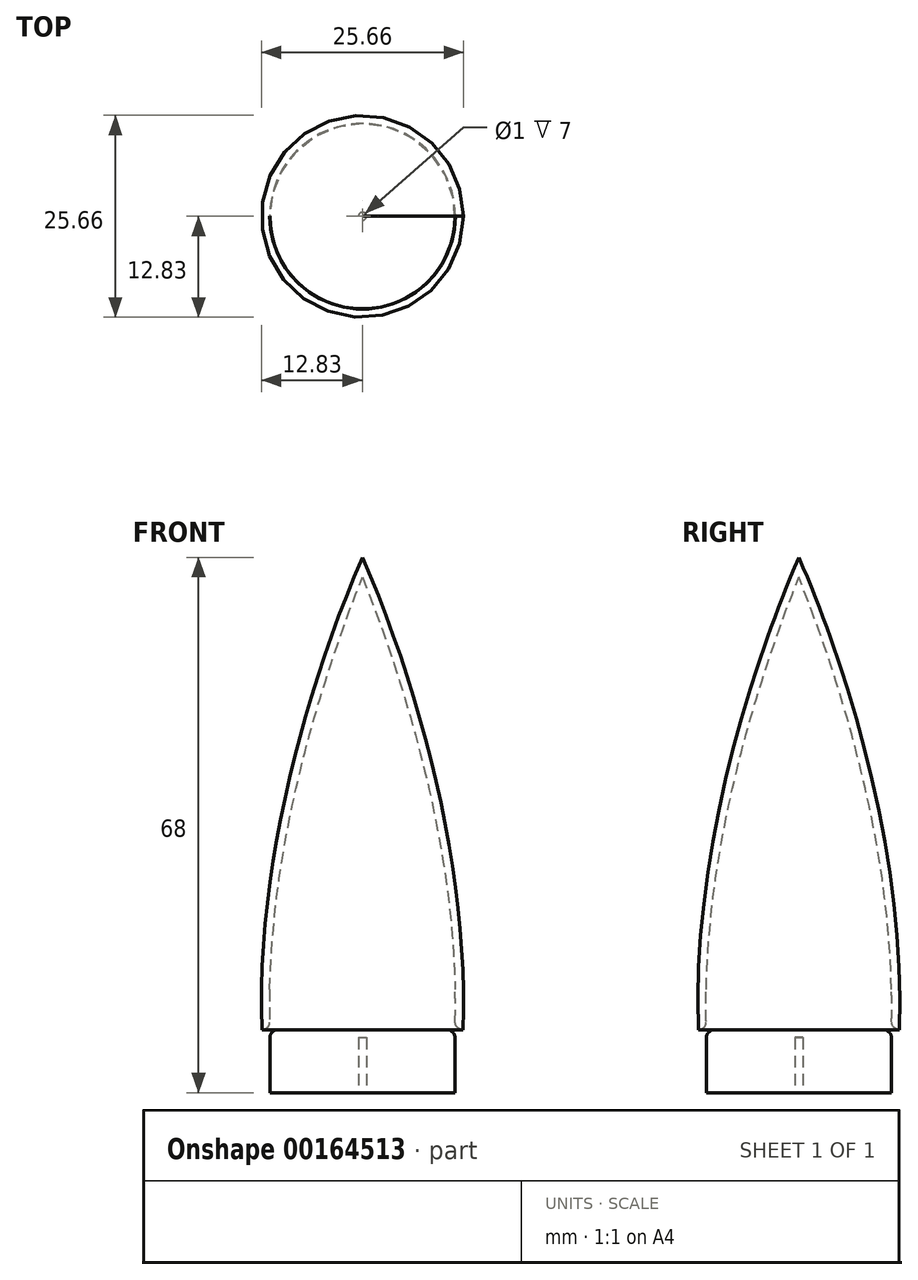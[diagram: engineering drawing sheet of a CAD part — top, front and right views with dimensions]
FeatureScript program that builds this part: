
annotation { "Feature Type Name" : "Feature", "Feature Type Description" : "" }
export const myFeature = defineFeature(function(context is Context, id is Id, definition is map)
    precondition{}
    {
        {
            var Q0;
            Q0=qCreatedBy(makeId("Front.planeOp"),FACE);
            var sketch = newSketch(context, id + "F0", { "sketchPlane" : qUnion([Q0])});
            skPoint(sketch, "E0.0", {"position": v(0, 0) * mm});
            skPoint(sketch, "E1.endSnap0", {"position": v(0, 8) * mm});
            skFitSpline(sketch, "E2", {"points": [v(0, 68) * mm, v(12.75, 8) * mm], "startDerivative": vector(23.82, -54.9) * mm, "endDerivative": vector(-2.44, -56.68) * mm});
            skLineSegment(sketch, "E3", {"start": v(6.61, 8) * mm, "end": v(12.75, 8) * mm});
            skLineSegment(sketch, "E4", {"start": v(0, 8) * mm, "end": v(6.77, 8) * mm});
            skLineSegment(sketch, "E5", {"start": v(11.75, 8) * mm, "end": v(11.75, 0) * mm});
            skLineSegment(sketch, "E6", {"start": v(11.75, 0) * mm, "end": v(0.5, 0) * mm});
            skLineSegment(sketch, "E7", {"start": v(0, 8) * mm, "end": v(0, 7) * mm});
            skLineSegment(sketch, "E8", {"start": v(0, 65.49) * mm, "end": v(0, 68) * mm});
            skFitSpline(sketch, "E9", {"points": [v(0, 65.49) * mm, v(11.75, 8) * mm], "startDerivative": vector(21.48, -54.4) * mm, "endDerivative": vector(-1.7, -57.32) * mm});
            skArc(sketch, "E10.filletArc", {"start": v(6.77, 8) * mm, "mid": v(10.34, 9.5) * mm, "end": v(11.77, 13.1) * mm});
            skLineSegment(sketch, "E11", {"start": v(0, 8) * mm, "end": v(0, 65.49) * mm, "construction": true});
            skLineSegment(sketch, "E12", {"start": v(0, 7) * mm, "end": v(0.5, 7) * mm});
            skLineSegment(sketch, "E13", {"start": v(0.5, 7) * mm, "end": v(0.5, 0) * mm});
            skSolve(sketch);
        }
        {
            var Q0;
            {var subQ1=sQuery(id+"F0.wireOp",EDGE,"E2");Q0=makeQuery(id+"F0.imprint","IMPRINT",FACE,{"disambiguationData":[TD([[makeQuery(id+"F0.imprint","IMPRINT",EDGE,{"derivedFrom":subQ1}),-1.0]])]});}
            var Q1;
            {var subQ0=sQuery(id+"F0.wireOp",EDGE,"E5");Q1=makeQuery(id+"F0.imprint","IMPRINT",FACE,{"disambiguationData":[TD([[makeQuery(id+"F0.imprint","IMPRINT",EDGE,{"derivedFrom":subQ0}),-1.0]])]});}
            var Q2;
            Q2=sQuery(id+"F0.wireOp",EDGE,"E11");
            revolve(context, id + "F1", {"entities" : qUnion([Q0, Q1]), "axis" : qUnion([Q2]), "revolveType" : RevolveType.FULL});
        }
        {
            var Q0;
            Q0=makeQuery(id+"F1.opRevolve","SWEPT_EDGE",EDGE,{"disambiguationData":[OSD([sQuery(id+"F0.wireOp",EDGE,"E3"),sQuery(id+"F0.wireOp",EDGE,"E5")])]});
            fillet(context, id + "F2", {"entities" : qUnion([Q0]), "radius" : 1 * mm, "tangentPropagation" : true, "allowEdgeOverflow" : false});
        }
    });
